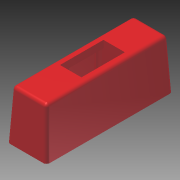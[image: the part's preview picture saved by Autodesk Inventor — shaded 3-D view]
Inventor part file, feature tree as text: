
AUTODESK INVENTOR PART (.ipt)
format: ipt  version: 2013 (Build 170138000, 138)  size: 326,144 bytes
history: native  units: in
note: dims shown in document units (in); Inventor stores cm internally (conversion verified against a paired STEP export)
features: sketch x11, plane x9, extrude x8, projected_geometry x6, fillet x5, other x2, mirror x2, thread x2, reference x2, hole x1, loft x1, pattern_linear x1, chamfer x1
ambient origin geometry x8: Origin, YZ Plane, XZ Plane, XY Plane, X Axis, Y Axis, Z Axis, Center Point
bodies: Solid1 (feature_tree)
feature tree (51):
  extrude  "Extrusion1"  Depth=0.039in
  fillet  "Fillet1"  Radius=0.028in
  sketch  "Sketch2"  dims[d6=0.04in d7=0.04in]
  extrude  "Extrusion3"  Depth=0.04in
  extrude  "Extrusion4"  Depth=0.028in
  fillet  "Fillet4"  Radius=0.028in
  fillet  "Fillet6"  Radius=0.539in
  plane  "Work Plane1"
  extrude  "Extrusion5"  Depth=0.02in
  hole  "Hole1"  [1 undecoded]
  plane  "Work Plane2"
  extrude  "Extrusion6"  Depth=0.5625in TaperAngle=0.0deg
  other  "Work Axis1"
  other  "Work Axis2"
  plane  "Work Plane4"
  mirror  "Mirror1"
  fillet  "Fillet7"  Radius=0.197in
  loft  "Loft1"
  plane  "Work Plane6"
  extrude  "Extrusion9"  Depth=0.374in TaperAngle=0.0deg
  extrude  "Extrusion10"  Depth=0.26in
  fillet  "Fillet9"  Radius=0.528in
  pattern_linear  "Rectangular Pattern1"  Spacing1=0.0in  [1 undecoded]
  plane  "Work Plane7"
  mirror  "Mirror2"
  plane  "Work Plane8"
  plane  "Work Plane9"
  extrude  "Extrusion12"  TaperAngle=0.0deg  [1 undecoded]
  chamfer  "Chamfer3"  [1 undecoded]
  thread  "Thread1"  [1 undecoded]
  thread  "Thread2"  [1 undecoded]
  sketch  "Sketch1"  dims[d0=0.598in d1=-0.0206in d2=0.039in d3=0.028in]
  projected_geometry  "Projected Loop1"
  sketch  "Sketch3"  dims[d8=0.04in d9=0.028in d10=0.028in d11=0.0in d14=0.539in d15=-0.0206in]
  sketch  "Sketch4"  dims[d16=0.059in d18=0.02in]
  reference  "Reference1"
  reference  "Reference2"
  sketch  "Sketch5"  dims[d19=0.479in d20=0.303in]
  projected_geometry  "Projected Loop2"
  sketch  "Sketch7"  dims[d21=0.157in d22=0.5625in d23=0.0in]
  projected_geometry  "Projected Loop4"
  projected_geometry  "Projected Loop5"
  plane  "Work Plane3"
  sketch  "Sketch10"  dims[d24=0.067in d25=0.75in d26=0.375in d27=0.25in d28=0.5635in d29=0.323in d30=0.0in d31=0.197in]
  sketch  "Sketch11"  dims[d32=0.073in d33=0.033in]
  projected_geometry  "Projected Loop8"
  plane  "Work Plane5"
  sketch  "Sketch13"  dims[d34=1.0in d35=0.0069in d36=0.0in d37=0.374in]
  sketch  "Sketch14"  dims[d43=0.02in d44=0.26in d45=0.528in]
  sketch  "Sketch16"  dims[d47=0.26in d48=0.0in d49=90.0deg d50=0.0in d51=90.0deg d63=-0.064in d64=0.316in d65=0.028in d66=0.0in d67=0.02in d68=0.112in d69=0.028in d70=0.0in d71=0.0155in d72=0.01in d73=0.7874in d75=0.354in d76=0.0in d88=0.0in d89=0.0197in d90=0.197in d91=0.099in d92=0.028in d93=0.0in d94=0.02in d95=0.112in d96=45.0deg d97=1.0in d98=0.0in d99=1.0in d100=0.0in]
  projected_geometry  "Projected Loop10"
note: 6 required parameter values undecoded (feature->parameter linkage not recoverable at this tier; creation-order binding heuristic only, values carry confidence <= 0.55)
